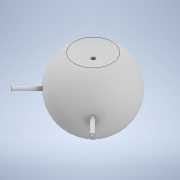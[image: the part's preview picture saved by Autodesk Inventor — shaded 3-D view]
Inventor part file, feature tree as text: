
AUTODESK INVENTOR PART (.ipt)
format: ipt  version: 2022 (Build 260153000, 153)  size: 186,368 bytes
history: native  units: in
note: dims shown in document units (in); Inventor stores cm internally (conversion verified against a paired STEP export)
features: sketch x9, extrude x5, revolve x4
ambient origin geometry x8: Origin, YZ Plane, XZ Plane, XY Plane, X Axis, Y Axis, Z Axis, Center Point
bodies: Body1 (feature_tree)
feature tree (18):
  revolve  "Revolution2"  Angle=90.0deg
  extrude  "Extrusion1"  Depth=0.932in TaperAngle=0.0deg
  revolve  "Revolution3"  [1 undecoded]
  extrude  "Extrusion2"  Depth=2.5in
  revolve  "Revolution4"  [1 undecoded]
  extrude  "Extrusion3"  Depth=1.25in
  extrude  "Extrusion4"  Depth=1.25in
  extrude  "Extrusion5"  Depth=4.0in TaperAngle=0.0deg
  revolve  "Revolution5"  [1 undecoded]
  sketch  "Sketch3"  dims[d3=2.5in d6=90.0deg]
  sketch  "Sketch5"  dims[d7=0.125in d8=0.932in d9=0.0in]
  sketch  "Sketch6"  dims[d10=1.25in d11=1.25in]
  sketch  "Sketch7"  dims[d12=1.3in d13=2.5in]
  sketch  "Sketch8"  dims[d14=90.0deg d15=0.932in d16=0.0in]
  sketch  "Sketch9"  dims[d17=1.3in d18=1.25in]
  sketch  "Sketch10"  dims[d19=1.25in d20=1.25in]
  sketch  "Sketch11"  dims[d21=90.0deg d22=4.0in d23=0.0in]
  sketch  "Sketch12"  dims[d24=0.125in d25=0.932in d26=0.0in d27=0.125in d28=0.932in d29=0.0in d30=0.7559in]
note: 3 required parameter values undecoded (feature->parameter linkage not recoverable at this tier; creation-order binding heuristic only, values carry confidence <= 0.55)
